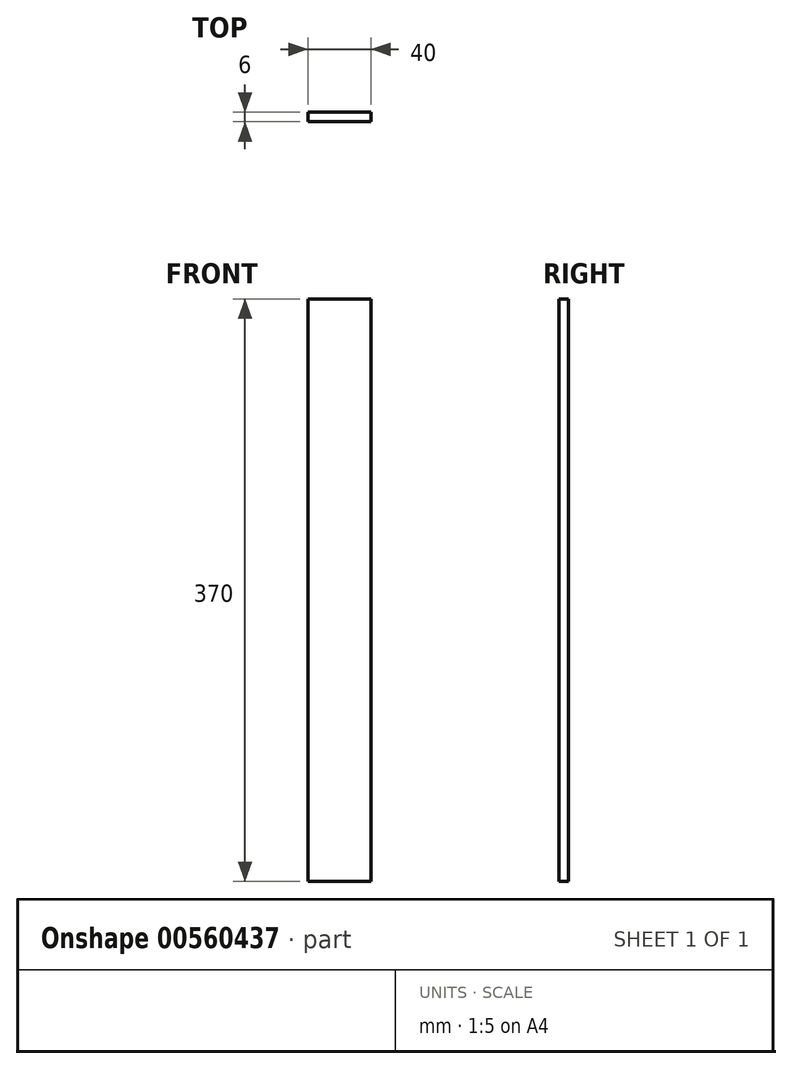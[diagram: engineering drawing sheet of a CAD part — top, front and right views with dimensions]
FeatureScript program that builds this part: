
annotation { "Feature Type Name" : "Feature", "Feature Type Description" : "" }
export const myFeature = defineFeature(function(context is Context, id is Id, definition is map)
    precondition{}
    {
        {
            var Q0;
            Q0=qCreatedBy(makeId("Front.planeOp"),FACE);
            var sketch = newSketch(context, id + "F0", { "sketchPlane" : qUnion([Q0])});
            skLineSegment(sketch, "E0.bottom", {"start": v(20, 185) * mm, "end": v(-20, 185) * mm});
            skLineSegment(sketch, "E0.top", {"start": v(20, -185) * mm, "end": v(-20, -185) * mm});
            skLineSegment(sketch, "E0.left", {"start": v(20, 185) * mm, "end": v(20, -185) * mm});
            skLineSegment(sketch, "E0.right", {"start": v(-20, 185) * mm, "end": v(-20, -185) * mm});
            skPoint(sketch, "E0.middle", {"position": v(0, 0) * mm});
            skSolve(sketch);
        }
        {
            var Q0;
            Q0=makeQuery(id+"F0.imprint","IMPRINT",FACE,{"disambiguationData":[TD([[makeQuery(id+"F0.imprint","IMPRINT",EDGE,{"derivedFrom":sQuery(id+"F0.wireOp",EDGE,"E0.bottom")}),1.0]])]});
            extrude(context, id + "F1", {"entities" : qUnion([Q0]), "endBound" : BoundingType.SYMMETRIC, "depth" : 6 * mm, "offsetDistance" : 25 * mm});
        }
    });
